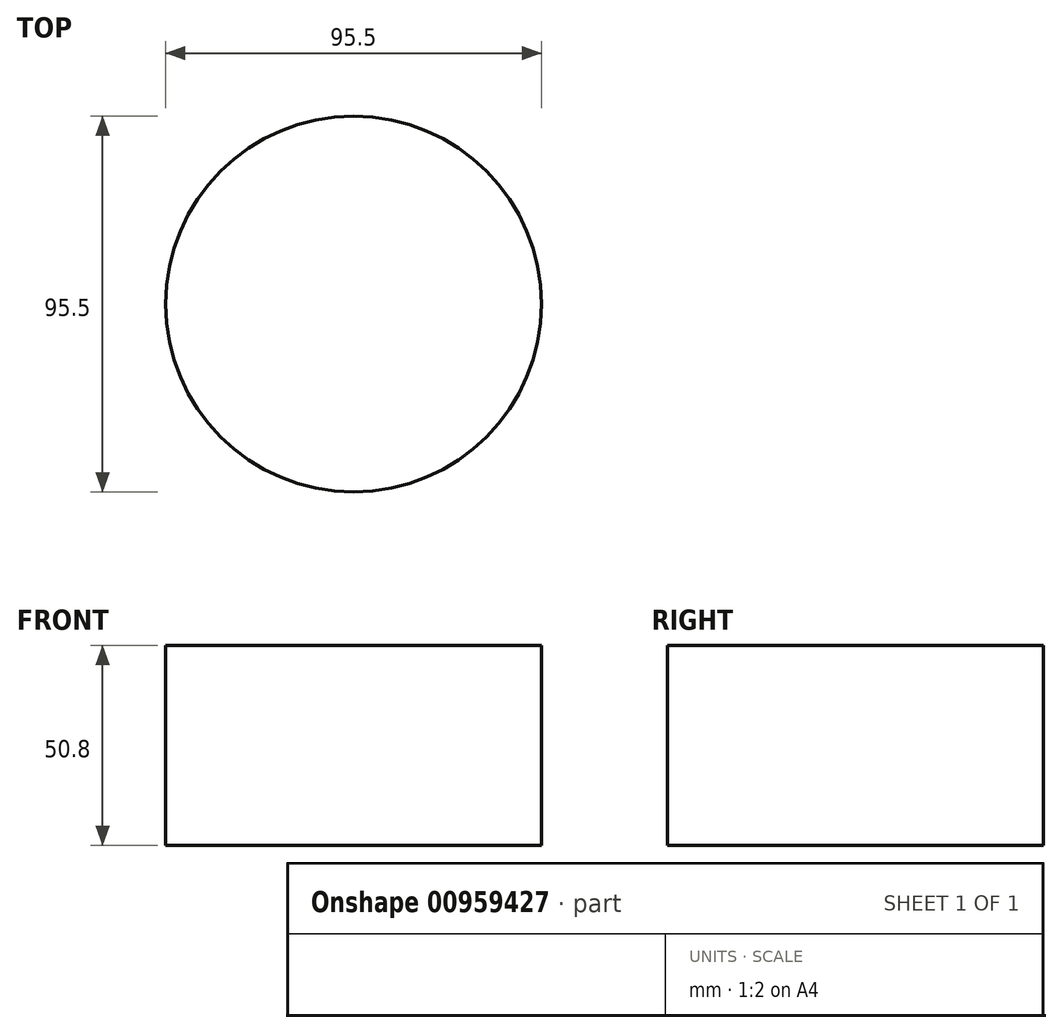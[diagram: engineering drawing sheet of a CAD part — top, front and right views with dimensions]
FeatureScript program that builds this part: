
annotation { "Feature Type Name" : "Feature", "Feature Type Description" : "" }
export const myFeature = defineFeature(function(context is Context, id is Id, definition is map)
    precondition{}
    {
        {
            var Q0;
            Q0=qCreatedBy(makeId("Top.planeOp"),FACE);
            var sketch = newSketch(context, id + "F0", { "sketchPlane" : qUnion([Q0])});
            skCircle(sketch, "E0", {"center": v(0, 0) * mm, "radius": 47.75 * mm});
            skSolve(sketch);
        }
        {
            var Q0;
            Q0 = qSketchRegion(id + "F0", true);
            extrude(context, id + "F1", {"entities" : qUnion([Q0]), "depth" : 50.8 * mm, "offsetDistance" : 25.4 * mm});
        }
    });
